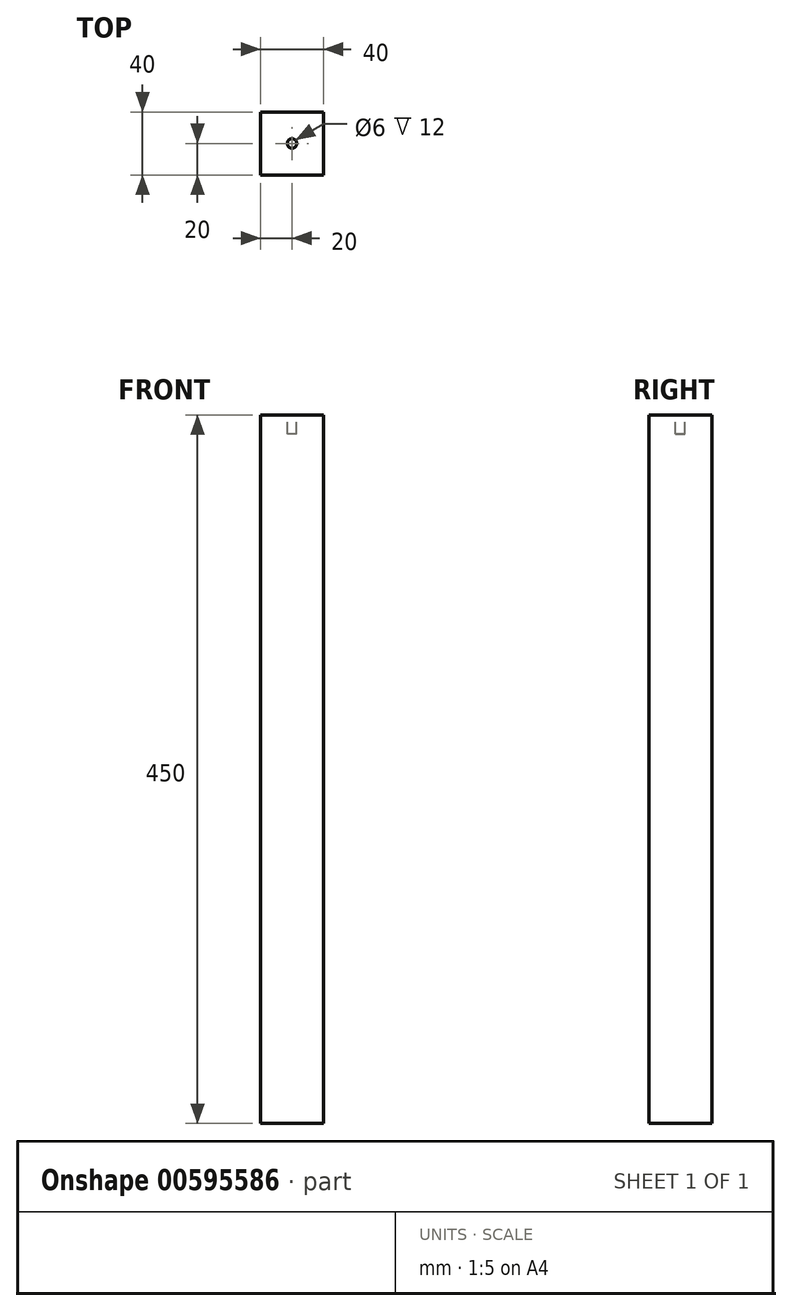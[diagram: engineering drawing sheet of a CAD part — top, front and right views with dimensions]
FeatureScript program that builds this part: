
annotation { "Feature Type Name" : "Feature", "Feature Type Description" : "" }
export const myFeature = defineFeature(function(context is Context, id is Id, definition is map)
    precondition{}
    {
        {
            var Q0;
            Q0=qCreatedBy(makeId("Top.planeOp"),FACE);
            var sketch = newSketch(context, id + "F0", { "sketchPlane" : qUnion([Q0])});
            skLineSegment(sketch, "E0.bottom", {"start": v(0, 0) * mm, "end": v(40, 0) * mm});
            skLineSegment(sketch, "E0.top", {"start": v(0, 40) * mm, "end": v(40, 40) * mm});
            skLineSegment(sketch, "E0.left", {"start": v(0, 0) * mm, "end": v(0, 40) * mm});
            skLineSegment(sketch, "E0.right", {"start": v(40, 0) * mm, "end": v(40, 40) * mm});
            skSolve(sketch);
        }
        {
            var Q0;
            Q0 = qSketchRegion(id + "F0", true);
            extrude(context, id + "F1", {"entities" : qUnion([Q0]), "depth" : 450 * mm, "offsetDistance" : 25 * mm});
        }
        {
            var Q0;
            Q0=makeQuery(id+"F1.opExtrude","CAP_FACE",FACE,{"disambiguationData":[OSD([sQuery(id+"F0.wireOp",EDGE,"E0.bottom"),sQuery(id+"F0.wireOp",EDGE,"E0.top"),sQuery(id+"F0.wireOp",EDGE,"E0.left"),sQuery(id+"F0.wireOp",EDGE,"E0.right")])],"isStart":false});
            var sketch = newSketch(context, id + "F2", { "sketchPlane" : qUnion([Q0])});
            skCircle(sketch, "E1", {"center": v(20, 20) * mm, "radius": 3 * mm});
            skPoint(sketch, "E1.centerSnap0", {"position": v(0, 20) * mm});
            skPoint(sketch, "E1.centerSnap1", {"position": v(20, 40) * mm});
            skSolve(sketch);
        }
        {
            var Q0;
            Q0 = qSketchRegion(id + "F2", true);
            extrude(context, id + "F3", {"entities" : qUnion([Q0]), "operationType" : NewBodyOperationType.REMOVE, "oppositeDirection" : true, "depth" : 12 * mm, "offsetDistance" : 25 * mm});
        }
    });
